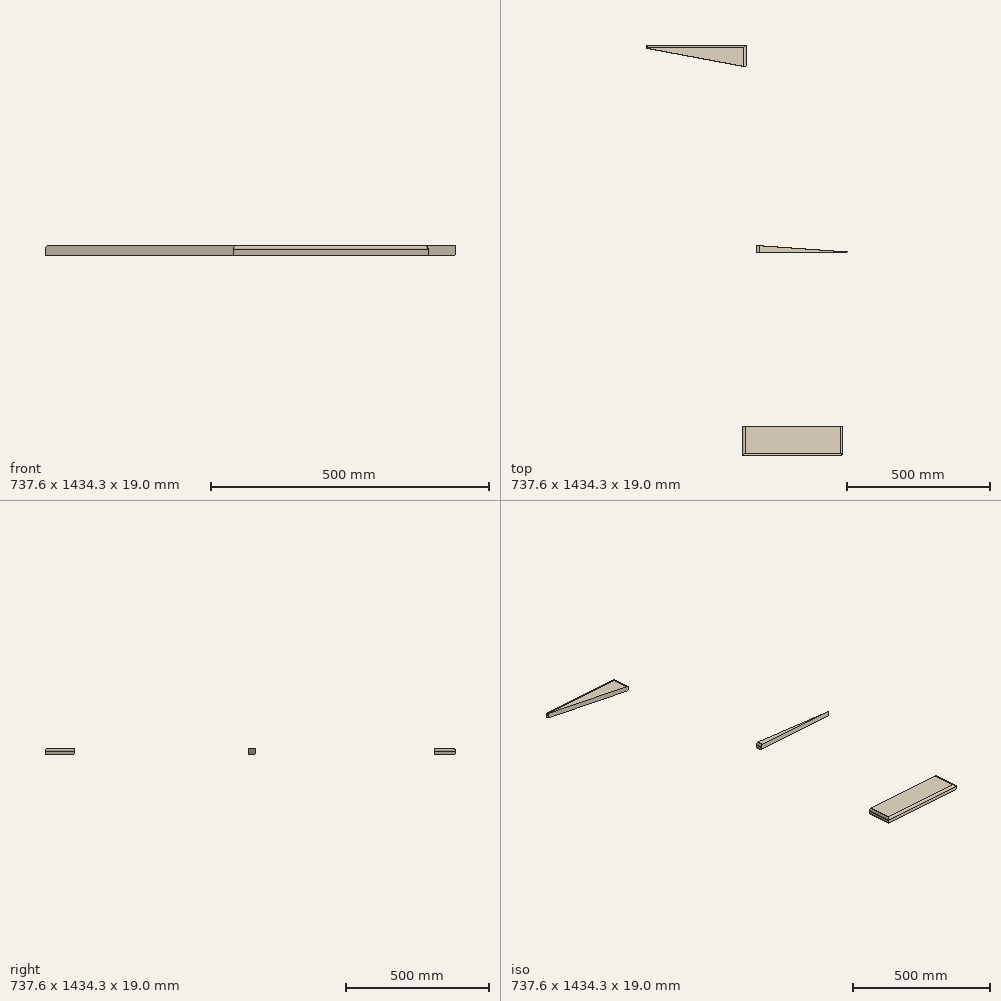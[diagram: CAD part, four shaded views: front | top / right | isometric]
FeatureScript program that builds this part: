
annotation { "Feature Type Name" : "Feature", "Feature Type Description" : "" }
export const myFeature = defineFeature(function(context is Context, id is Id, definition is map)
    precondition{}
    {
        {
            var Q0;
            Q0=qCreatedBy(makeId("Top.planeOp"),FACE);
            var sketch = newSketch(context, id + "F0", { "sketchPlane" : qUnion([Q0])});
            skLineSegment(sketch, "E0.bottom", {"start": v(-4722.67, -3198.06) * mm, "end": v(-4372.67, -3198.06) * mm});
            skLineSegment(sketch, "E0.top", {"start": v(-4722.67, -3298.06) * mm, "end": v(-4372.67, -3298.06) * mm});
            skLineSegment(sketch, "E0.left", {"start": v(-4722.67, -3198.06) * mm, "end": v(-4722.67, -3298.06) * mm});
            skLineSegment(sketch, "E0.right", {"start": v(-4372.67, -3198.06) * mm, "end": v(-4372.67, -3298.06) * mm});
            skSolve(sketch);
        }
        {
            var Q0;
            Q0=qCreatedBy(makeId("Top.planeOp"),FACE);
            var sketch = newSketch(context, id + "F1", { "sketchPlane" : qUnion([Q0])});
            skLineSegment(sketch, "E1.bottom", {"start": v(-5061.16, -1863.77) * mm, "end": v(-4711.16, -1863.77) * mm});
            skLineSegment(sketch, "E1.left", {"start": v(-5061.16, -1863.77) * mm, "end": v(-5061.16, -1938.77) * mm});
            skLineSegment(sketch, "E1.right", {"start": v(-4711.16, -1863.77) * mm, "end": v(-4711.16, -1938.77) * mm});
            skLineSegment(sketch, "E2", {"start": v(-5111.16, -1863.77) * mm, "end": v(-4711.16, -1938.77) * mm});
            skSolve(sketch);
        }
        {
            var Q0;
            Q0=qCreatedBy(makeId("Top.planeOp"),FACE);
            var sketch = newSketch(context, id + "F2", { "sketchPlane" : qUnion([Q0])});
            skLineSegment(sketch, "E3.top", {"start": v(-4673.52, -2588.57) * mm, "end": v(-4323.52, -2588.57) * mm});
            skLineSegment(sketch, "E3.left", {"start": v(-4673.52, -2563.57) * mm, "end": v(-4673.52, -2588.57) * mm});
            skLineSegment(sketch, "E4", {"start": v(-4673.52, -2563.57) * mm, "end": v(-4323.52, -2588.57) * mm});
            skSolve(sketch);
        }
        {
            var Q0;
            Q0 = qSketchRegion(id + "F0", true);
            extrude(context, id + "F3", {"entities" : qUnion([Q0]), "depth" : 19 * mm, "offsetDistance" : 25 * mm});
        }
        {
            var Q0;
            Q0 = qSketchRegion(id + "F1", true);
            extrude(context, id + "F4", {"entities" : qUnion([Q0]), "depth" : 19 * mm, "offsetDistance" : 25 * mm});
        }
        {
            var Q0;
            Q0 = qSketchRegion(id + "F2", true);
            extrude(context, id + "F5", {"entities" : qUnion([Q0]), "depth" : 19 * mm, "offsetDistance" : 25 * mm});
        }
        {
            var Q0;
            Q0=makeQuery(id+"F4.opExtrude","CAP_EDGE",EDGE,{"disambiguationData":[OSD([sQuery(id+"F1.wireOp",EDGE,"E1.left")])],"isStart":false});
            var Q1;
            Q1=makeQuery(id+"F4.opExtrude","CAP_EDGE",EDGE,{"disambiguationData":[OSD([sQuery(id+"F1.wireOp",EDGE,"E1.bottom")])],"isStart":false});
            var Q2;
            Q2=makeQuery(id+"F4.opExtrude","CAP_EDGE",EDGE,{"disambiguationData":[OSD([sQuery(id+"F1.wireOp",EDGE,"E1.right")])],"isStart":false});
            var Q3;
            Q3=makeQuery(id+"F5.opExtrude","CAP_EDGE",EDGE,{"disambiguationData":[OSD([sQuery(id+"F2.wireOp",EDGE,"E3.right")])],"isStart":false});
            var Q4;
            Q4=makeQuery(id+"F5.opExtrude","CAP_EDGE",EDGE,{"disambiguationData":[OSD([sQuery(id+"F2.wireOp",EDGE,"E3.left")])],"isStart":false});
            var Q5;
            Q5=makeQuery(id+"F3.opExtrude","CAP_EDGE",EDGE,{"disambiguationData":[OSD([sQuery(id+"F0.wireOp",EDGE,"E0.left")])],"isStart":false});
            var Q6;
            Q6=makeQuery(id+"F3.opExtrude","CAP_EDGE",EDGE,{"disambiguationData":[OSD([sQuery(id+"F0.wireOp",EDGE,"E0.right")])],"isStart":false});
            var Q7;
            Q7=makeQuery(id+"F3.opExtrude","CAP_EDGE",EDGE,{"disambiguationData":[OSD([sQuery(id+"F0.wireOp",EDGE,"E0.top")])],"isStart":false});
            fillet(context, id + "F6", {"entities" : qUnion([Q0, Q1, Q2, Q3, Q4, Q5, Q6, Q7]), "radius" : 8 * mm, "tangentPropagation" : true, "allowEdgeOverflow" : false});
        }
    });
